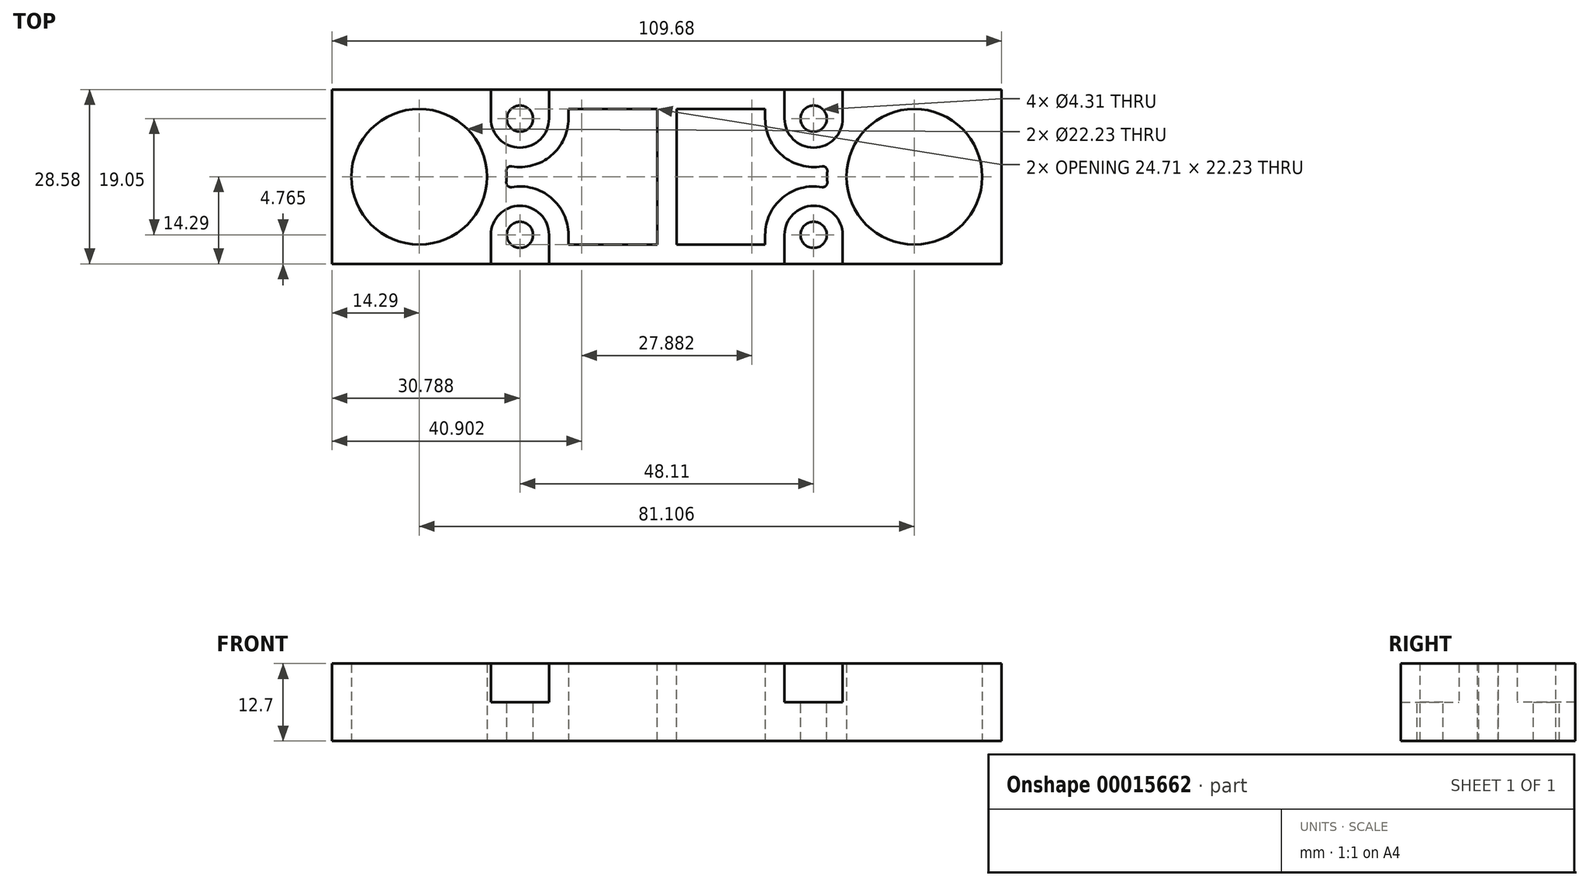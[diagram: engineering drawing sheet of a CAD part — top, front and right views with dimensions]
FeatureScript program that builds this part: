
annotation { "Feature Type Name" : "Feature", "Feature Type Description" : "" }
export const myFeature = defineFeature(function(context is Context, id is Id, definition is map)
    precondition{}
    {
        {
            var Q0;
            Q0=qCreatedBy(makeId("Top.planeOp"),FACE);
            var sketch = newSketch(context, id + "F0", { "sketchPlane" : qUnion([Q0])});
            skCircle(sketch, "E0", {"center": v(0, 0) * mm, "radius": 11.11 * mm});
            skLineSegment(sketch, "E1", {"start": v(0, 0) * mm, "end": v(81.1, 0) * mm, "construction": true});
            skLineSegment(sketch, "E2.left", {"start": v(-14.29, 14.29) * mm, "end": v(-14.29, -14.29) * mm});
            skLineSegment(sketch, "E2.right", {"start": v(95.4, 14.29) * mm, "end": v(95.4, -14.29) * mm});
            skPoint(sketch, "E2.middle", {"position": v(40.55, 0) * mm});
            skLineSegment(sketch, "E3", {"start": v(81.1, 0) * mm, "end": v(95.4, 0) * mm, "construction": true});
            skLineSegment(sketch, "E4", {"start": v(0, 0) * mm, "end": v(-14.29, 0) * mm, "construction": true});
            skCircle(sketch, "E5", {"center": v(81.1, 0) * mm, "radius": 11.11 * mm});
            skLineSegment(sketch, "E6", {"start": v(-14.29, 14.29) * mm, "end": v(11.74, 14.29) * mm});
            skLineSegment(sketch, "E7", {"start": v(95.4, 14.29) * mm, "end": v(69.37, 14.29) * mm});
            skLineSegment(sketch, "E8.bottom", {"start": v(11.74, 14.29) * mm, "end": v(21.26, 14.29) * mm, "construction": true});
            skLineSegment(sketch, "E8.top", {"start": v(11.74, 9.53) * mm, "end": v(21.26, 9.53) * mm, "construction": true});
            skLineSegment(sketch, "E8.left", {"start": v(11.74, 14.29) * mm, "end": v(11.74, 9.52) * mm});
            skLineSegment(sketch, "E8.right", {"start": v(21.26, 14.29) * mm, "end": v(21.26, 9.52) * mm});
            skLineSegment(sketch, "E9.bottom", {"start": v(69.37, 14.29) * mm, "end": v(59.85, 14.29) * mm, "construction": true});
            skLineSegment(sketch, "E9.top", {"start": v(69.37, 9.52) * mm, "end": v(59.85, 9.52) * mm, "construction": true});
            skLineSegment(sketch, "E9.left", {"start": v(69.37, 14.29) * mm, "end": v(69.37, 9.52) * mm});
            skLineSegment(sketch, "E9.right", {"start": v(59.85, 14.29) * mm, "end": v(59.85, 9.53) * mm});
            skCircle(sketch, "E10", {"center": v(16.5, 9.53) * mm, "radius": 7.94 * mm, "construction": true});
            skArc(sketch, "E11", {"start": v(21.26, 9.52) * mm, "mid": v(16.5, 14.29) * mm, "end": v(11.74, 9.53) * mm, "construction": true});
            skArc(sketch, "E12", {"start": v(11.74, 9.52) * mm, "mid": v(16.5, 4.76) * mm, "end": v(21.26, 9.52) * mm});
            skArc(sketch, "E13", {"start": v(59.85, 9.53) * mm, "mid": v(64.6, 4.76) * mm, "end": v(69.37, 9.52) * mm});
            skLineSegment(sketch, "E14", {"start": v(21.26, 14.29) * mm, "end": v(59.85, 14.29) * mm});
            skLineSegment(sketch, "E15", {"start": v(-14.29, -14.29) * mm, "end": v(11.74, -14.29) * mm});
            skLineSegment(sketch, "E16", {"start": v(95.4, -14.29) * mm, "end": v(69.37, -14.29) * mm});
            skLineSegment(sketch, "E17.bottom", {"start": v(11.74, -14.29) * mm, "end": v(21.26, -14.29) * mm, "construction": true});
            skLineSegment(sketch, "E17.top", {"start": v(11.74, -9.52) * mm, "end": v(21.26, -9.52) * mm, "construction": true});
            skLineSegment(sketch, "E17.left", {"start": v(11.74, -14.29) * mm, "end": v(11.74, -9.52) * mm});
            skLineSegment(sketch, "E17.right", {"start": v(21.26, -14.29) * mm, "end": v(21.26, -9.53) * mm});
            skLineSegment(sketch, "E18.bottom", {"start": v(69.37, -14.29) * mm, "end": v(59.85, -14.29) * mm, "construction": true});
            skLineSegment(sketch, "E18.top", {"start": v(69.37, -9.52) * mm, "end": v(59.85, -9.52) * mm, "construction": true});
            skLineSegment(sketch, "E18.left", {"start": v(69.37, -14.29) * mm, "end": v(69.37, -9.52) * mm});
            skLineSegment(sketch, "E18.right", {"start": v(59.85, -14.29) * mm, "end": v(59.85, -9.52) * mm});
            skLineSegment(sketch, "E19", {"start": v(21.26, -14.29) * mm, "end": v(59.85, -14.29) * mm});
            skArc(sketch, "E20", {"start": v(21.26, -9.53) * mm, "mid": v(16.5, -4.76) * mm, "end": v(11.74, -9.52) * mm});
            skArc(sketch, "E21", {"start": v(69.37, -9.52) * mm, "mid": v(64.6, -4.76) * mm, "end": v(59.85, -9.52) * mm});
            skSolve(sketch);
        }
        {
            var Q0;
            Q0=qSketchRegion(id+"F0",true);
            extrude(context, id + "F1", {"entities" : qUnion([Q0]), "depth" : 6.35 * mm});
        }
        {
            var Q0;
            Q0=makeQuery(id+"F1.opExtrude","CAP_FACE",FACE,{"disambiguationData":[OSD([sQuery(id+"F0.wireOp",EDGE,"E0"),sQuery(id+"F0.wireOp",EDGE,"E2.left"),sQuery(id+"F0.wireOp",EDGE,"E2.right"),sQuery(id+"F0.wireOp",EDGE,"E5"),sQuery(id+"F0.wireOp",EDGE,"E6"),sQuery(id+"F0.wireOp",EDGE,"E7"),sQuery(id+"F0.wireOp",EDGE,"E8.left"),sQuery(id+"F0.wireOp",EDGE,"E8.right"),sQuery(id+"F0.wireOp",EDGE,"E9.left"),sQuery(id+"F0.wireOp",EDGE,"E9.right"),sQuery(id+"F0.wireOp",EDGE,"E12"),sQuery(id+"F0.wireOp",EDGE,"E13"),sQuery(id+"F0.wireOp",EDGE,"E14"),sQuery(id+"F0.wireOp",EDGE,"E15"),sQuery(id+"F0.wireOp",EDGE,"E16"),sQuery(id+"F0.wireOp",EDGE,"E17.left"),sQuery(id+"F0.wireOp",EDGE,"E17.right"),sQuery(id+"F0.wireOp",EDGE,"E18.left"),sQuery(id+"F0.wireOp",EDGE,"E18.right"),sQuery(id+"F0.wireOp",EDGE,"E19"),sQuery(id+"F0.wireOp",EDGE,"E20"),sQuery(id+"F0.wireOp",EDGE,"E21")])],"isStart":false});
            shell(context, id + "F2", {"entities" : qUnion([Q0]), "thickness" : 3.17 * mm});
        }
        {
            var Q0;
            Q0=makeQuery(id+"F2.opShell","OFFSET_FACE",FACE,{"disambiguationData":[OSD([sQuery(id+"F0.wireOp",EDGE,"E0"),sQuery(id+"F0.wireOp",EDGE,"E2.left"),sQuery(id+"F0.wireOp",EDGE,"E2.right"),sQuery(id+"F0.wireOp",EDGE,"E5"),sQuery(id+"F0.wireOp",EDGE,"E6"),sQuery(id+"F0.wireOp",EDGE,"E7"),sQuery(id+"F0.wireOp",EDGE,"E8.left"),sQuery(id+"F0.wireOp",EDGE,"E8.right"),sQuery(id+"F0.wireOp",EDGE,"E9.left"),sQuery(id+"F0.wireOp",EDGE,"E9.right"),sQuery(id+"F0.wireOp",EDGE,"E12"),sQuery(id+"F0.wireOp",EDGE,"E13"),sQuery(id+"F0.wireOp",EDGE,"E14"),sQuery(id+"F0.wireOp",EDGE,"E15"),sQuery(id+"F0.wireOp",EDGE,"E16"),sQuery(id+"F0.wireOp",EDGE,"E17.left"),sQuery(id+"F0.wireOp",EDGE,"E17.right"),sQuery(id+"F0.wireOp",EDGE,"E18.left"),sQuery(id+"F0.wireOp",EDGE,"E18.right"),sQuery(id+"F0.wireOp",EDGE,"E19"),sQuery(id+"F0.wireOp",EDGE,"E20"),sQuery(id+"F0.wireOp",EDGE,"E21")]),OD(0.0)]});
            var Q1;
            Q1=makeQuery(id+"F2.opShell","OFFSET_FACE",FACE,{"disambiguationData":[OSD([sQuery(id+"F0.wireOp",EDGE,"E0"),sQuery(id+"F0.wireOp",EDGE,"E2.left"),sQuery(id+"F0.wireOp",EDGE,"E2.right"),sQuery(id+"F0.wireOp",EDGE,"E5"),sQuery(id+"F0.wireOp",EDGE,"E6"),sQuery(id+"F0.wireOp",EDGE,"E7"),sQuery(id+"F0.wireOp",EDGE,"E8.left"),sQuery(id+"F0.wireOp",EDGE,"E8.right"),sQuery(id+"F0.wireOp",EDGE,"E9.left"),sQuery(id+"F0.wireOp",EDGE,"E9.right"),sQuery(id+"F0.wireOp",EDGE,"E12"),sQuery(id+"F0.wireOp",EDGE,"E13"),sQuery(id+"F0.wireOp",EDGE,"E14"),sQuery(id+"F0.wireOp",EDGE,"E15"),sQuery(id+"F0.wireOp",EDGE,"E16"),sQuery(id+"F0.wireOp",EDGE,"E17.left"),sQuery(id+"F0.wireOp",EDGE,"E17.right"),sQuery(id+"F0.wireOp",EDGE,"E18.left"),sQuery(id+"F0.wireOp",EDGE,"E18.right"),sQuery(id+"F0.wireOp",EDGE,"E19"),sQuery(id+"F0.wireOp",EDGE,"E20"),sQuery(id+"F0.wireOp",EDGE,"E21")]),OD(3.0)]});
            var Q2;
            Q2=makeQuery(id+"F2.opShell","OFFSET_FACE",FACE,{"disambiguationData":[OSD([sQuery(id+"F0.wireOp",EDGE,"E0"),sQuery(id+"F0.wireOp",EDGE,"E2.left"),sQuery(id+"F0.wireOp",EDGE,"E2.right"),sQuery(id+"F0.wireOp",EDGE,"E5"),sQuery(id+"F0.wireOp",EDGE,"E6"),sQuery(id+"F0.wireOp",EDGE,"E7"),sQuery(id+"F0.wireOp",EDGE,"E8.left"),sQuery(id+"F0.wireOp",EDGE,"E8.right"),sQuery(id+"F0.wireOp",EDGE,"E9.left"),sQuery(id+"F0.wireOp",EDGE,"E9.right"),sQuery(id+"F0.wireOp",EDGE,"E12"),sQuery(id+"F0.wireOp",EDGE,"E13"),sQuery(id+"F0.wireOp",EDGE,"E14"),sQuery(id+"F0.wireOp",EDGE,"E15"),sQuery(id+"F0.wireOp",EDGE,"E16"),sQuery(id+"F0.wireOp",EDGE,"E17.left"),sQuery(id+"F0.wireOp",EDGE,"E17.right"),sQuery(id+"F0.wireOp",EDGE,"E18.left"),sQuery(id+"F0.wireOp",EDGE,"E18.right"),sQuery(id+"F0.wireOp",EDGE,"E19"),sQuery(id+"F0.wireOp",EDGE,"E20"),sQuery(id+"F0.wireOp",EDGE,"E21")]),OD(4.0)]});
            var Q3;
            Q3=makeQuery(id+"F2.opShell","OFFSET_FACE",FACE,{"disambiguationData":[OSD([sQuery(id+"F0.wireOp",EDGE,"E0"),sQuery(id+"F0.wireOp",EDGE,"E2.left"),sQuery(id+"F0.wireOp",EDGE,"E2.right"),sQuery(id+"F0.wireOp",EDGE,"E5"),sQuery(id+"F0.wireOp",EDGE,"E6"),sQuery(id+"F0.wireOp",EDGE,"E7"),sQuery(id+"F0.wireOp",EDGE,"E8.left"),sQuery(id+"F0.wireOp",EDGE,"E8.right"),sQuery(id+"F0.wireOp",EDGE,"E9.left"),sQuery(id+"F0.wireOp",EDGE,"E9.right"),sQuery(id+"F0.wireOp",EDGE,"E12"),sQuery(id+"F0.wireOp",EDGE,"E13"),sQuery(id+"F0.wireOp",EDGE,"E14"),sQuery(id+"F0.wireOp",EDGE,"E15"),sQuery(id+"F0.wireOp",EDGE,"E16"),sQuery(id+"F0.wireOp",EDGE,"E17.left"),sQuery(id+"F0.wireOp",EDGE,"E17.right"),sQuery(id+"F0.wireOp",EDGE,"E18.left"),sQuery(id+"F0.wireOp",EDGE,"E18.right"),sQuery(id+"F0.wireOp",EDGE,"E19"),sQuery(id+"F0.wireOp",EDGE,"E20"),sQuery(id+"F0.wireOp",EDGE,"E21")]),OD(1.0)]});
            var Q4;
            Q4=makeQuery(id+"F1.opExtrude","CAP_FACE",FACE,{"disambiguationData":[OSD([sQuery(id+"F0.wireOp",EDGE,"E0"),sQuery(id+"F0.wireOp",EDGE,"E2.left"),sQuery(id+"F0.wireOp",EDGE,"E2.right"),sQuery(id+"F0.wireOp",EDGE,"E5"),sQuery(id+"F0.wireOp",EDGE,"E6"),sQuery(id+"F0.wireOp",EDGE,"E7"),sQuery(id+"F0.wireOp",EDGE,"E8.left"),sQuery(id+"F0.wireOp",EDGE,"E8.right"),sQuery(id+"F0.wireOp",EDGE,"E9.left"),sQuery(id+"F0.wireOp",EDGE,"E9.right"),sQuery(id+"F0.wireOp",EDGE,"E12"),sQuery(id+"F0.wireOp",EDGE,"E13"),sQuery(id+"F0.wireOp",EDGE,"E14"),sQuery(id+"F0.wireOp",EDGE,"E15"),sQuery(id+"F0.wireOp",EDGE,"E16"),sQuery(id+"F0.wireOp",EDGE,"E17.left"),sQuery(id+"F0.wireOp",EDGE,"E17.right"),sQuery(id+"F0.wireOp",EDGE,"E18.left"),sQuery(id+"F0.wireOp",EDGE,"E18.right"),sQuery(id+"F0.wireOp",EDGE,"E19"),sQuery(id+"F0.wireOp",EDGE,"E20"),sQuery(id+"F0.wireOp",EDGE,"E21")])],"isStart":false});
            extrude(context, id + "F3", {"entities" : qUnion([Q0, Q1, Q2, Q3]), "operationType" : NewBodyOperationType.ADD, "endBound" : BoundingType.UP_TO_SURFACE, "endBoundEntityFace" : qUnion([Q4]), "depth" : 25.4 * mm});
        }
        {
            var Q0;
            Q0=makeQuery(id+"F2.opShell","OFFSET_FACE",FACE,{"disambiguationData":[OSD([sQuery(id+"F0.wireOp",EDGE,"E0"),sQuery(id+"F0.wireOp",EDGE,"E2.left"),sQuery(id+"F0.wireOp",EDGE,"E2.right"),sQuery(id+"F0.wireOp",EDGE,"E5"),sQuery(id+"F0.wireOp",EDGE,"E6"),sQuery(id+"F0.wireOp",EDGE,"E7"),sQuery(id+"F0.wireOp",EDGE,"E8.left"),sQuery(id+"F0.wireOp",EDGE,"E8.right"),sQuery(id+"F0.wireOp",EDGE,"E9.left"),sQuery(id+"F0.wireOp",EDGE,"E9.right"),sQuery(id+"F0.wireOp",EDGE,"E12"),sQuery(id+"F0.wireOp",EDGE,"E13"),sQuery(id+"F0.wireOp",EDGE,"E14"),sQuery(id+"F0.wireOp",EDGE,"E15"),sQuery(id+"F0.wireOp",EDGE,"E16"),sQuery(id+"F0.wireOp",EDGE,"E17.left"),sQuery(id+"F0.wireOp",EDGE,"E17.right"),sQuery(id+"F0.wireOp",EDGE,"E18.left"),sQuery(id+"F0.wireOp",EDGE,"E18.right"),sQuery(id+"F0.wireOp",EDGE,"E19"),sQuery(id+"F0.wireOp",EDGE,"E20"),sQuery(id+"F0.wireOp",EDGE,"E21")]),OD(2.0)]});
            var Q1;
            Q1=makeQuery(id+"F1.opExtrude","CAP_FACE",FACE,{"disambiguationData":[OSD([sQuery(id+"F0.wireOp",EDGE,"E0"),sQuery(id+"F0.wireOp",EDGE,"E2.left"),sQuery(id+"F0.wireOp",EDGE,"E2.right"),sQuery(id+"F0.wireOp",EDGE,"E5"),sQuery(id+"F0.wireOp",EDGE,"E6"),sQuery(id+"F0.wireOp",EDGE,"E7"),sQuery(id+"F0.wireOp",EDGE,"E8.left"),sQuery(id+"F0.wireOp",EDGE,"E8.right"),sQuery(id+"F0.wireOp",EDGE,"E9.left"),sQuery(id+"F0.wireOp",EDGE,"E9.right"),sQuery(id+"F0.wireOp",EDGE,"E12"),sQuery(id+"F0.wireOp",EDGE,"E13"),sQuery(id+"F0.wireOp",EDGE,"E14"),sQuery(id+"F0.wireOp",EDGE,"E15"),sQuery(id+"F0.wireOp",EDGE,"E16"),sQuery(id+"F0.wireOp",EDGE,"E17.left"),sQuery(id+"F0.wireOp",EDGE,"E17.right"),sQuery(id+"F0.wireOp",EDGE,"E18.left"),sQuery(id+"F0.wireOp",EDGE,"E18.right"),sQuery(id+"F0.wireOp",EDGE,"E19"),sQuery(id+"F0.wireOp",EDGE,"E20"),sQuery(id+"F0.wireOp",EDGE,"E21")])],"isStart":true});
            extrude(context, id + "F4", {"entities" : qUnion([Q0]), "operationType" : NewBodyOperationType.REMOVE, "endBound" : BoundingType.UP_TO_SURFACE, "oppositeDirection" : true, "endBoundEntityFace" : qUnion([Q1]), "depth" : 25.4 * mm});
        }
        {
            var Q0;
            Q0=makeQuery(id+"F1.opExtrude","CAP_FACE",FACE,{"disambiguationData":[OSD([sQuery(id+"F0.wireOp",EDGE,"E0"),sQuery(id+"F0.wireOp",EDGE,"E2.left"),sQuery(id+"F0.wireOp",EDGE,"E2.right"),sQuery(id+"F0.wireOp",EDGE,"E5"),sQuery(id+"F0.wireOp",EDGE,"E6"),sQuery(id+"F0.wireOp",EDGE,"E7"),sQuery(id+"F0.wireOp",EDGE,"E8.left"),sQuery(id+"F0.wireOp",EDGE,"E8.right"),sQuery(id+"F0.wireOp",EDGE,"E9.left"),sQuery(id+"F0.wireOp",EDGE,"E9.right"),sQuery(id+"F0.wireOp",EDGE,"E12"),sQuery(id+"F0.wireOp",EDGE,"E13"),sQuery(id+"F0.wireOp",EDGE,"E14"),sQuery(id+"F0.wireOp",EDGE,"E15"),sQuery(id+"F0.wireOp",EDGE,"E16"),sQuery(id+"F0.wireOp",EDGE,"E17.left"),sQuery(id+"F0.wireOp",EDGE,"E17.right"),sQuery(id+"F0.wireOp",EDGE,"E18.left"),sQuery(id+"F0.wireOp",EDGE,"E18.right"),sQuery(id+"F0.wireOp",EDGE,"E19"),sQuery(id+"F0.wireOp",EDGE,"E20"),sQuery(id+"F0.wireOp",EDGE,"E21")])],"isStart":true});
            var sketch = newSketch(context, id + "F5", { "sketchPlane" : qUnion([Q0])});
            skLineSegment(sketch, "E22.bottom", {"start": v(11.74, -14.29) * mm, "end": v(69.37, -14.29) * mm});
            skLineSegment(sketch, "E22.top", {"start": v(11.74, 14.29) * mm, "end": v(69.37, 14.29) * mm});
            skLineSegment(sketch, "E22.left", {"start": v(11.74, -14.29) * mm, "end": v(11.74, 14.29) * mm, "construction": true});
            skLineSegment(sketch, "E22.right", {"start": v(69.37, -14.29) * mm, "end": v(69.37, 14.29) * mm, "construction": true});
            skCircle(sketch, "E23", {"center": v(16.5, 9.52) * mm, "radius": 2.15 * mm});
            skCircle(sketch, "E24", {"center": v(16.5, -9.53) * mm, "radius": 2.15 * mm});
            skCircle(sketch, "E25", {"center": v(64.6, 9.52) * mm, "radius": 2.15 * mm});
            skCircle(sketch, "E26", {"center": v(64.6, -9.53) * mm, "radius": 2.15 * mm});
            skSolve(sketch);
        }
        {
            var Q0;
            {var subQ19=sQuery(id+"F0.wireOp",EDGE,"E0");var subQ20=makeQuery(id+"F1.opExtrude","CAP_EDGE",EDGE,{"disambiguationData":[OSD([subQ19])],"isStart":true});Q0=makeQuery(id+"F5.imprint","IMPRINT",FACE,{"disambiguationData":[TD([[makeQuery(id+"F5.imprint","IMPRINT",EDGE,{"derivedFrom":subQ20}),1.0]])]});}
            var Q1;
            Q1=makeQuery(id+"F5.imprint","IMPRINT",FACE,{"disambiguationData":[TD([[makeQuery(id+"F5.imprint","IMPRINT",EDGE,{"derivedFrom":sQuery(id+"F5.wireOp",EDGE,"E24")}),-1.0]])]});
            var Q2;
            Q2=makeQuery(id+"F5.imprint","IMPRINT",FACE,{"disambiguationData":[TD([[makeQuery(id+"F5.imprint","IMPRINT",EDGE,{"derivedFrom":sQuery(id+"F5.wireOp",EDGE,"E26")}),-1.0]])]});
            var Q3;
            Q3=makeQuery(id+"F5.imprint","IMPRINT",FACE,{"disambiguationData":[TD([[makeQuery(id+"F5.imprint","IMPRINT",EDGE,{"derivedFrom":sQuery(id+"F5.wireOp",EDGE,"E25")}),-1.0]])]});
            var Q4;
            Q4=makeQuery(id+"F5.imprint","IMPRINT",FACE,{"disambiguationData":[TD([[makeQuery(id+"F5.imprint","IMPRINT",EDGE,{"derivedFrom":sQuery(id+"F5.wireOp",EDGE,"E23")}),-1.0]])]});
            extrude(context, id + "F6", {"entities" : qUnion([Q0, Q1, Q2, Q3, Q4]), "operationType" : NewBodyOperationType.ADD, "depth" : 6.35 * mm});
        }
        {
            var Q0;
            {var subQ0=sQuery(id+"F0.wireOp",EDGE,"E21");var subQ1=sQuery(id+"F0.wireOp",EDGE,"E20");var subQ2=sQuery(id+"F0.wireOp",EDGE,"E19");var subQ3=sQuery(id+"F0.wireOp",EDGE,"E18.right");var subQ4=sQuery(id+"F0.wireOp",EDGE,"E18.left");var subQ5=sQuery(id+"F0.wireOp",EDGE,"E17.right");var subQ6=sQuery(id+"F0.wireOp",EDGE,"E17.left");var subQ7=sQuery(id+"F0.wireOp",EDGE,"E16");var subQ8=sQuery(id+"F0.wireOp",EDGE,"E15");var subQ9=sQuery(id+"F0.wireOp",EDGE,"E14");var subQ10=sQuery(id+"F0.wireOp",EDGE,"E13");var subQ11=sQuery(id+"F0.wireOp",EDGE,"E12");var subQ12=sQuery(id+"F0.wireOp",EDGE,"E9.right");var subQ13=sQuery(id+"F0.wireOp",EDGE,"E9.left");var subQ14=sQuery(id+"F0.wireOp",EDGE,"E8.right");var subQ15=sQuery(id+"F0.wireOp",EDGE,"E8.left");var subQ16=sQuery(id+"F0.wireOp",EDGE,"E7");var subQ17=sQuery(id+"F0.wireOp",EDGE,"E6");var subQ18=sQuery(id+"F0.wireOp",EDGE,"E5");var subQ19=sQuery(id+"F0.wireOp",EDGE,"E2.right");var subQ20=sQuery(id+"F0.wireOp",EDGE,"E2.left");var subQ21=sQuery(id+"F0.wireOp",EDGE,"E0");Q0=makeQuery(id+"F3.boolean.opBoolean","MERGE",FACE,{"derivedFrom":[makeQuery(id+"F1.opExtrude","CAP_FACE",FACE,{"disambiguationData":[OSD([subQ21,subQ20,subQ19,subQ18,subQ17,subQ16,subQ15,subQ14,subQ13,subQ12,subQ11,subQ10,subQ9,subQ8,subQ7,subQ6,subQ5,subQ4,subQ3,subQ2,subQ1,subQ0])],"isStart":false}),makeQuery(id+"F3.opExtrude","CAP_FACE",FACE,{"disambiguationData":[OSD([subQ21,subQ20,subQ19,subQ18,subQ17,subQ16,subQ15,subQ14,subQ13,subQ12,subQ11,subQ10,subQ9,subQ8,subQ7,subQ6,subQ5,subQ4,subQ3,subQ2,subQ1,subQ0]),ownerDisambiguation([makeQuery(id+"F3.opExtrude","SWEPT_BODY",BODY,{"disambiguationData":[OSD([subQ21,subQ20,subQ19,subQ18,subQ17,subQ16,subQ15,subQ14,subQ13,subQ12,subQ11,subQ10,subQ9,subQ8,subQ7,subQ6,subQ5,subQ4,subQ3,subQ2,subQ1,subQ0]),TDD([makeQuery(id+"F2.opShell","OFFSET_FACE",FACE,{"disambiguationData":[OSD([subQ21,subQ20,subQ19,subQ18,subQ17,subQ16,subQ15,subQ14,subQ13,subQ12,subQ11,subQ10,subQ9,subQ8,subQ7,subQ6,subQ5,subQ4,subQ3,subQ2,subQ1,subQ0]),OD(0.0)]})])]})])],"isStart":false}),makeQuery(id+"F3.opExtrude","CAP_FACE",FACE,{"disambiguationData":[OSD([subQ21,subQ20,subQ19,subQ18,subQ17,subQ16,subQ15,subQ14,subQ13,subQ12,subQ11,subQ10,subQ9,subQ8,subQ7,subQ6,subQ5,subQ4,subQ3,subQ2,subQ1,subQ0]),ownerDisambiguation([makeQuery(id+"F3.opExtrude","SWEPT_BODY",BODY,{"disambiguationData":[OSD([subQ21,subQ20,subQ19,subQ18,subQ17,subQ16,subQ15,subQ14,subQ13,subQ12,subQ11,subQ10,subQ9,subQ8,subQ7,subQ6,subQ5,subQ4,subQ3,subQ2,subQ1,subQ0]),TDD([makeQuery(id+"F2.opShell","OFFSET_FACE",FACE,{"disambiguationData":[OSD([subQ21,subQ20,subQ19,subQ18,subQ17,subQ16,subQ15,subQ14,subQ13,subQ12,subQ11,subQ10,subQ9,subQ8,subQ7,subQ6,subQ5,subQ4,subQ3,subQ2,subQ1,subQ0]),OD(1.0)]})])]})])],"isStart":false}),makeQuery(id+"F3.opExtrude","CAP_FACE",FACE,{"disambiguationData":[OSD([subQ21,subQ20,subQ19,subQ18,subQ17,subQ16,subQ15,subQ14,subQ13,subQ12,subQ11,subQ10,subQ9,subQ8,subQ7,subQ6,subQ5,subQ4,subQ3,subQ2,subQ1,subQ0]),ownerDisambiguation([makeQuery(id+"F3.opExtrude","SWEPT_BODY",BODY,{"disambiguationData":[OSD([subQ21,subQ20,subQ19,subQ18,subQ17,subQ16,subQ15,subQ14,subQ13,subQ12,subQ11,subQ10,subQ9,subQ8,subQ7,subQ6,subQ5,subQ4,subQ3,subQ2,subQ1,subQ0]),TDD([makeQuery(id+"F2.opShell","OFFSET_FACE",FACE,{"disambiguationData":[OSD([subQ21,subQ20,subQ19,subQ18,subQ17,subQ16,subQ15,subQ14,subQ13,subQ12,subQ11,subQ10,subQ9,subQ8,subQ7,subQ6,subQ5,subQ4,subQ3,subQ2,subQ1,subQ0]),OD(3.0)]})])]})])],"isStart":false}),makeQuery(id+"F3.opExtrude","CAP_FACE",FACE,{"disambiguationData":[OSD([subQ21,subQ20,subQ19,subQ18,subQ17,subQ16,subQ15,subQ14,subQ13,subQ12,subQ11,subQ10,subQ9,subQ8,subQ7,subQ6,subQ5,subQ4,subQ3,subQ2,subQ1,subQ0]),ownerDisambiguation([makeQuery(id+"F3.opExtrude","SWEPT_BODY",BODY,{"disambiguationData":[OSD([subQ21,subQ20,subQ19,subQ18,subQ17,subQ16,subQ15,subQ14,subQ13,subQ12,subQ11,subQ10,subQ9,subQ8,subQ7,subQ6,subQ5,subQ4,subQ3,subQ2,subQ1,subQ0]),TDD([makeQuery(id+"F2.opShell","OFFSET_FACE",FACE,{"disambiguationData":[OSD([subQ21,subQ20,subQ19,subQ18,subQ17,subQ16,subQ15,subQ14,subQ13,subQ12,subQ11,subQ10,subQ9,subQ8,subQ7,subQ6,subQ5,subQ4,subQ3,subQ2,subQ1,subQ0]),OD(4.0)]})])]})])],"isStart":false})]});}
            var sketch = newSketch(context, id + "F7", { "sketchPlane" : qUnion([Q0])});
            skLineSegment(sketch, "E27.bottom", {"start": v(38.97, 11.11) * mm, "end": v(42.14, 11.11) * mm});
            skLineSegment(sketch, "E27.top", {"start": v(38.97, -11.11) * mm, "end": v(42.14, -11.11) * mm});
            skLineSegment(sketch, "E27.left", {"start": v(38.97, 11.11) * mm, "end": v(38.97, -11.11) * mm});
            skLineSegment(sketch, "E27.right", {"start": v(42.14, 11.11) * mm, "end": v(42.14, -11.11) * mm});
            skPoint(sketch, "E28", {"position": v(40.55, 11.11) * mm});
            skSolve(sketch);
        }
        {
            var Q0;
            Q0=qSketchRegion(id+"F7",true);
            var Q1;
            Q1=makeQuery(id+"F6.opExtrude","CAP_FACE",FACE,{"disambiguationData":[OSD([sQuery(id+"F0.wireOp",EDGE,"E0"),sQuery(id+"F0.wireOp",EDGE,"E2.left"),sQuery(id+"F0.wireOp",EDGE,"E2.right"),sQuery(id+"F0.wireOp",EDGE,"E5"),sQuery(id+"F0.wireOp",EDGE,"E6"),sQuery(id+"F0.wireOp",EDGE,"E7"),sQuery(id+"F0.wireOp",EDGE,"E8.left"),sQuery(id+"F0.wireOp",EDGE,"E8.right"),sQuery(id+"F0.wireOp",EDGE,"E9.left"),sQuery(id+"F0.wireOp",EDGE,"E9.right"),sQuery(id+"F0.wireOp",EDGE,"E12"),sQuery(id+"F0.wireOp",EDGE,"E13"),sQuery(id+"F0.wireOp",EDGE,"E14"),sQuery(id+"F0.wireOp",EDGE,"E15"),sQuery(id+"F0.wireOp",EDGE,"E16"),sQuery(id+"F0.wireOp",EDGE,"E17.left"),sQuery(id+"F0.wireOp",EDGE,"E17.right"),sQuery(id+"F0.wireOp",EDGE,"E18.left"),sQuery(id+"F0.wireOp",EDGE,"E18.right"),sQuery(id+"F0.wireOp",EDGE,"E19"),sQuery(id+"F0.wireOp",EDGE,"E20"),sQuery(id+"F0.wireOp",EDGE,"E21"),sQuery(id+"F5.wireOp",EDGE,"E22.bottom"),sQuery(id+"F5.wireOp",EDGE,"E22.top"),sQuery(id+"F5.wireOp",EDGE,"E23"),sQuery(id+"F5.wireOp",EDGE,"E24"),sQuery(id+"F5.wireOp",EDGE,"E25"),sQuery(id+"F5.wireOp",EDGE,"E26")])],"isStart":false});
            extrude(context, id + "F8", {"entities" : qUnion([Q0]), "operationType" : NewBodyOperationType.ADD, "endBound" : BoundingType.UP_TO_SURFACE, "oppositeDirection" : true, "endBoundEntityFace" : qUnion([Q1]), "depth" : 25.4 * mm});
        }
        {
            var Q0;
            {var subQ0=sQuery(id+"F0.wireOp",EDGE,"E0");var subQ1=sQuery(id+"F0.wireOp",EDGE,"E21");var subQ2=sQuery(id+"F0.wireOp",EDGE,"E20");var subQ3=sQuery(id+"F0.wireOp",EDGE,"E19");var subQ4=sQuery(id+"F0.wireOp",EDGE,"E18.right");var subQ5=sQuery(id+"F0.wireOp",EDGE,"E18.left");var subQ6=sQuery(id+"F0.wireOp",EDGE,"E17.right");var subQ7=sQuery(id+"F0.wireOp",EDGE,"E17.left");var subQ8=sQuery(id+"F0.wireOp",EDGE,"E16");var subQ9=sQuery(id+"F0.wireOp",EDGE,"E15");var subQ10=sQuery(id+"F0.wireOp",EDGE,"E14");var subQ11=sQuery(id+"F0.wireOp",EDGE,"E13");var subQ12=sQuery(id+"F0.wireOp",EDGE,"E12");var subQ13=sQuery(id+"F0.wireOp",EDGE,"E9.right");var subQ14=sQuery(id+"F0.wireOp",EDGE,"E9.left");var subQ15=sQuery(id+"F0.wireOp",EDGE,"E8.right");var subQ16=sQuery(id+"F0.wireOp",EDGE,"E8.left");var subQ17=sQuery(id+"F0.wireOp",EDGE,"E7");var subQ18=sQuery(id+"F0.wireOp",EDGE,"E6");var subQ19=sQuery(id+"F0.wireOp",EDGE,"E5");var subQ20=sQuery(id+"F0.wireOp",EDGE,"E2.right");var subQ21=sQuery(id+"F0.wireOp",EDGE,"E2.left");var subQ22=makeQuery(id+"F1.opExtrude","CAP_FACE",FACE,{"disambiguationData":[OSD([subQ0,subQ21,subQ20,subQ19,subQ18,subQ17,subQ16,subQ15,subQ14,subQ13,subQ12,subQ11,subQ10,subQ9,subQ8,subQ7,subQ6,subQ5,subQ4,subQ3,subQ2,subQ1])],"isStart":true});var subQ23=makeQuery(id+"F1.opExtrude","SWEPT_FACE",FACE,{"disambiguationData":[OSD([subQ12])]});var subQ24=makeQuery(id+"F1.opExtrude","SWEPT_FACE",FACE,{"disambiguationData":[OSD([subQ0])]});Q0=makeQuery(id+"F6.boolean.opBoolean","MERGE",EDGE,{"derivedFrom":[makeQuery(id+"F4.boolean.opBoolean","MERGE",EDGE,{"derivedFrom":[makeQuery(id+"F2.opShell","TWEAK_EDGE",EDGE,{"derivedFrom":[subQ24,subQ23]}),makeQuery(id+"F4.opExtrude","SWEPT_EDGE",EDGE,{"disambiguationData":[OSD([subQ0,subQ21,subQ20,subQ19,subQ18,subQ17,subQ16,subQ15,subQ14,subQ13,subQ12,subQ11,subQ10,subQ9,subQ8,subQ7,subQ6,subQ5,subQ4,subQ3,subQ2,subQ1]),TDD([makeQuery(id+"F2.opShell","TWEAK_VERTEX",VERTEX,{"derivedFrom":[subQ24,subQ22,subQ23]})])]})]}),makeQuery(id+"F6.opExtrude","SWEPT_EDGE",EDGE,{"disambiguationData":[OSD([subQ0,subQ21,subQ20,subQ19,subQ18,subQ17,subQ16,subQ15,subQ14,subQ13,subQ12,subQ11,subQ10,subQ9,subQ8,subQ7,subQ6,subQ5,subQ4,subQ3,subQ2,subQ1]),TDD([makeQuery(id+"F5.imprint","INTERSECT",VERTEX,{"derivedFrom":[makeQuery(id+"F4.boolean.opBoolean","COPY",EDGE,{"derivedFrom":makeQuery(id+"F4.opExtrude","TWEAK_EDGE",EDGE,{"derivedFrom":[subQ22,makeQuery(id+"F2.opShell","OFFSET_EDGE",EDGE,{"disambiguationData":[OSD([subQ12]),TDD([makeQuery(id+"F1.opExtrude","CAP_EDGE",EDGE,{"disambiguationData":[OSD([subQ12])],"isStart":true})])]})]})}),makeQuery(id+"F4.boolean.opBoolean","COPY",EDGE,{"derivedFrom":makeQuery(id+"F4.opExtrude","TWEAK_EDGE",EDGE,{"derivedFrom":[subQ22,makeQuery(id+"F2.opShell","OFFSET_EDGE",EDGE,{"disambiguationData":[OSD([subQ0]),TDD([makeQuery(id+"F1.opExtrude","CAP_EDGE",EDGE,{"disambiguationData":[OSD([subQ0])],"isStart":true})]),OD(0.0)]})]})})]})])]})]});}
            var Q1;
            {var subQ0=sQuery(id+"F0.wireOp",EDGE,"E0");var subQ1=sQuery(id+"F0.wireOp",EDGE,"E21");var subQ2=sQuery(id+"F0.wireOp",EDGE,"E20");var subQ3=sQuery(id+"F0.wireOp",EDGE,"E19");var subQ4=sQuery(id+"F0.wireOp",EDGE,"E18.right");var subQ5=sQuery(id+"F0.wireOp",EDGE,"E18.left");var subQ6=sQuery(id+"F0.wireOp",EDGE,"E17.right");var subQ7=sQuery(id+"F0.wireOp",EDGE,"E17.left");var subQ8=sQuery(id+"F0.wireOp",EDGE,"E16");var subQ9=sQuery(id+"F0.wireOp",EDGE,"E15");var subQ10=sQuery(id+"F0.wireOp",EDGE,"E14");var subQ11=sQuery(id+"F0.wireOp",EDGE,"E13");var subQ12=sQuery(id+"F0.wireOp",EDGE,"E12");var subQ13=sQuery(id+"F0.wireOp",EDGE,"E9.right");var subQ14=sQuery(id+"F0.wireOp",EDGE,"E9.left");var subQ15=sQuery(id+"F0.wireOp",EDGE,"E8.right");var subQ16=sQuery(id+"F0.wireOp",EDGE,"E8.left");var subQ17=sQuery(id+"F0.wireOp",EDGE,"E7");var subQ18=sQuery(id+"F0.wireOp",EDGE,"E6");var subQ19=sQuery(id+"F0.wireOp",EDGE,"E5");var subQ20=sQuery(id+"F0.wireOp",EDGE,"E2.right");var subQ21=sQuery(id+"F0.wireOp",EDGE,"E2.left");var subQ22=makeQuery(id+"F1.opExtrude","CAP_FACE",FACE,{"disambiguationData":[OSD([subQ0,subQ21,subQ20,subQ19,subQ18,subQ17,subQ16,subQ15,subQ14,subQ13,subQ12,subQ11,subQ10,subQ9,subQ8,subQ7,subQ6,subQ5,subQ4,subQ3,subQ2,subQ1])],"isStart":true});var subQ23=makeQuery(id+"F1.opExtrude","SWEPT_FACE",FACE,{"disambiguationData":[OSD([subQ2])]});var subQ24=makeQuery(id+"F1.opExtrude","SWEPT_FACE",FACE,{"disambiguationData":[OSD([subQ0])]});Q1=makeQuery(id+"F6.boolean.opBoolean","MERGE",EDGE,{"derivedFrom":[makeQuery(id+"F4.boolean.opBoolean","MERGE",EDGE,{"derivedFrom":[makeQuery(id+"F2.opShell","TWEAK_EDGE",EDGE,{"derivedFrom":[subQ24,subQ23]}),makeQuery(id+"F4.opExtrude","SWEPT_EDGE",EDGE,{"disambiguationData":[OSD([subQ0,subQ21,subQ20,subQ19,subQ18,subQ17,subQ16,subQ15,subQ14,subQ13,subQ12,subQ11,subQ10,subQ9,subQ8,subQ7,subQ6,subQ5,subQ4,subQ3,subQ2,subQ1]),TDD([makeQuery(id+"F2.opShell","TWEAK_VERTEX",VERTEX,{"derivedFrom":[subQ24,subQ22,subQ23]})])]})]}),makeQuery(id+"F6.opExtrude","SWEPT_EDGE",EDGE,{"disambiguationData":[OSD([subQ0,subQ21,subQ20,subQ19,subQ18,subQ17,subQ16,subQ15,subQ14,subQ13,subQ12,subQ11,subQ10,subQ9,subQ8,subQ7,subQ6,subQ5,subQ4,subQ3,subQ2,subQ1]),TDD([makeQuery(id+"F5.imprint","INTERSECT",VERTEX,{"derivedFrom":[makeQuery(id+"F4.boolean.opBoolean","COPY",EDGE,{"derivedFrom":makeQuery(id+"F4.opExtrude","TWEAK_EDGE",EDGE,{"derivedFrom":[subQ22,makeQuery(id+"F2.opShell","OFFSET_EDGE",EDGE,{"disambiguationData":[OSD([subQ2]),TDD([makeQuery(id+"F1.opExtrude","CAP_EDGE",EDGE,{"disambiguationData":[OSD([subQ2])],"isStart":true})])]})]})}),makeQuery(id+"F4.boolean.opBoolean","COPY",EDGE,{"derivedFrom":makeQuery(id+"F4.opExtrude","TWEAK_EDGE",EDGE,{"derivedFrom":[subQ22,makeQuery(id+"F2.opShell","OFFSET_EDGE",EDGE,{"disambiguationData":[OSD([subQ0]),TDD([makeQuery(id+"F1.opExtrude","CAP_EDGE",EDGE,{"disambiguationData":[OSD([subQ0])],"isStart":true})]),OD(0.0)]})]})})]})])]})]});}
            var Q2;
            {var subQ0=sQuery(id+"F0.wireOp",EDGE,"E5");var subQ1=sQuery(id+"F0.wireOp",EDGE,"E21");var subQ2=sQuery(id+"F0.wireOp",EDGE,"E20");var subQ3=sQuery(id+"F0.wireOp",EDGE,"E19");var subQ4=sQuery(id+"F0.wireOp",EDGE,"E18.right");var subQ5=sQuery(id+"F0.wireOp",EDGE,"E18.left");var subQ6=sQuery(id+"F0.wireOp",EDGE,"E17.right");var subQ7=sQuery(id+"F0.wireOp",EDGE,"E17.left");var subQ8=sQuery(id+"F0.wireOp",EDGE,"E16");var subQ9=sQuery(id+"F0.wireOp",EDGE,"E15");var subQ10=sQuery(id+"F0.wireOp",EDGE,"E14");var subQ11=sQuery(id+"F0.wireOp",EDGE,"E13");var subQ12=sQuery(id+"F0.wireOp",EDGE,"E12");var subQ13=sQuery(id+"F0.wireOp",EDGE,"E9.right");var subQ14=sQuery(id+"F0.wireOp",EDGE,"E9.left");var subQ15=sQuery(id+"F0.wireOp",EDGE,"E8.right");var subQ16=sQuery(id+"F0.wireOp",EDGE,"E8.left");var subQ17=sQuery(id+"F0.wireOp",EDGE,"E7");var subQ18=sQuery(id+"F0.wireOp",EDGE,"E6");var subQ19=sQuery(id+"F0.wireOp",EDGE,"E2.right");var subQ20=sQuery(id+"F0.wireOp",EDGE,"E2.left");var subQ21=sQuery(id+"F0.wireOp",EDGE,"E0");var subQ22=makeQuery(id+"F1.opExtrude","CAP_FACE",FACE,{"disambiguationData":[OSD([subQ21,subQ20,subQ19,subQ0,subQ18,subQ17,subQ16,subQ15,subQ14,subQ13,subQ12,subQ11,subQ10,subQ9,subQ8,subQ7,subQ6,subQ5,subQ4,subQ3,subQ2,subQ1])],"isStart":true});var subQ23=makeQuery(id+"F1.opExtrude","SWEPT_FACE",FACE,{"disambiguationData":[OSD([subQ11])]});var subQ24=makeQuery(id+"F1.opExtrude","SWEPT_FACE",FACE,{"disambiguationData":[OSD([subQ0])]});Q2=makeQuery(id+"F6.boolean.opBoolean","MERGE",EDGE,{"derivedFrom":[makeQuery(id+"F4.boolean.opBoolean","MERGE",EDGE,{"derivedFrom":[makeQuery(id+"F2.opShell","TWEAK_EDGE",EDGE,{"derivedFrom":[subQ24,subQ23]}),makeQuery(id+"F4.opExtrude","SWEPT_EDGE",EDGE,{"disambiguationData":[OSD([subQ21,subQ20,subQ19,subQ0,subQ18,subQ17,subQ16,subQ15,subQ14,subQ13,subQ12,subQ11,subQ10,subQ9,subQ8,subQ7,subQ6,subQ5,subQ4,subQ3,subQ2,subQ1]),TDD([makeQuery(id+"F2.opShell","TWEAK_VERTEX",VERTEX,{"derivedFrom":[subQ22,subQ24,subQ23]})])]})]}),makeQuery(id+"F6.opExtrude","SWEPT_EDGE",EDGE,{"disambiguationData":[OSD([subQ21,subQ20,subQ19,subQ0,subQ18,subQ17,subQ16,subQ15,subQ14,subQ13,subQ12,subQ11,subQ10,subQ9,subQ8,subQ7,subQ6,subQ5,subQ4,subQ3,subQ2,subQ1]),TDD([makeQuery(id+"F5.imprint","INTERSECT",VERTEX,{"derivedFrom":[makeQuery(id+"F4.boolean.opBoolean","COPY",EDGE,{"derivedFrom":makeQuery(id+"F4.opExtrude","TWEAK_EDGE",EDGE,{"derivedFrom":[subQ22,makeQuery(id+"F2.opShell","OFFSET_EDGE",EDGE,{"disambiguationData":[OSD([subQ11]),TDD([makeQuery(id+"F1.opExtrude","CAP_EDGE",EDGE,{"disambiguationData":[OSD([subQ11])],"isStart":true})])]})]})}),makeQuery(id+"F4.boolean.opBoolean","COPY",EDGE,{"derivedFrom":makeQuery(id+"F4.opExtrude","TWEAK_EDGE",EDGE,{"derivedFrom":[subQ22,makeQuery(id+"F2.opShell","OFFSET_EDGE",EDGE,{"disambiguationData":[OSD([subQ0]),TDD([makeQuery(id+"F1.opExtrude","CAP_EDGE",EDGE,{"disambiguationData":[OSD([subQ0])],"isStart":true})]),OD(0.0)]})]})})]})])]})]});}
            var Q3;
            {var subQ0=sQuery(id+"F0.wireOp",EDGE,"E5");var subQ1=sQuery(id+"F0.wireOp",EDGE,"E21");var subQ2=sQuery(id+"F0.wireOp",EDGE,"E20");var subQ3=sQuery(id+"F0.wireOp",EDGE,"E19");var subQ4=sQuery(id+"F0.wireOp",EDGE,"E18.right");var subQ5=sQuery(id+"F0.wireOp",EDGE,"E18.left");var subQ6=sQuery(id+"F0.wireOp",EDGE,"E17.right");var subQ7=sQuery(id+"F0.wireOp",EDGE,"E17.left");var subQ8=sQuery(id+"F0.wireOp",EDGE,"E16");var subQ9=sQuery(id+"F0.wireOp",EDGE,"E15");var subQ10=sQuery(id+"F0.wireOp",EDGE,"E14");var subQ11=sQuery(id+"F0.wireOp",EDGE,"E13");var subQ12=sQuery(id+"F0.wireOp",EDGE,"E12");var subQ13=sQuery(id+"F0.wireOp",EDGE,"E9.right");var subQ14=sQuery(id+"F0.wireOp",EDGE,"E9.left");var subQ15=sQuery(id+"F0.wireOp",EDGE,"E8.right");var subQ16=sQuery(id+"F0.wireOp",EDGE,"E8.left");var subQ17=sQuery(id+"F0.wireOp",EDGE,"E7");var subQ18=sQuery(id+"F0.wireOp",EDGE,"E6");var subQ19=sQuery(id+"F0.wireOp",EDGE,"E2.right");var subQ20=sQuery(id+"F0.wireOp",EDGE,"E2.left");var subQ21=sQuery(id+"F0.wireOp",EDGE,"E0");var subQ22=makeQuery(id+"F1.opExtrude","CAP_FACE",FACE,{"disambiguationData":[OSD([subQ21,subQ20,subQ19,subQ0,subQ18,subQ17,subQ16,subQ15,subQ14,subQ13,subQ12,subQ11,subQ10,subQ9,subQ8,subQ7,subQ6,subQ5,subQ4,subQ3,subQ2,subQ1])],"isStart":true});var subQ23=makeQuery(id+"F1.opExtrude","SWEPT_FACE",FACE,{"disambiguationData":[OSD([subQ1])]});var subQ24=makeQuery(id+"F1.opExtrude","SWEPT_FACE",FACE,{"disambiguationData":[OSD([subQ0])]});Q3=makeQuery(id+"F6.boolean.opBoolean","MERGE",EDGE,{"derivedFrom":[makeQuery(id+"F4.boolean.opBoolean","MERGE",EDGE,{"derivedFrom":[makeQuery(id+"F2.opShell","TWEAK_EDGE",EDGE,{"derivedFrom":[subQ24,subQ23]}),makeQuery(id+"F4.opExtrude","SWEPT_EDGE",EDGE,{"disambiguationData":[OSD([subQ21,subQ20,subQ19,subQ0,subQ18,subQ17,subQ16,subQ15,subQ14,subQ13,subQ12,subQ11,subQ10,subQ9,subQ8,subQ7,subQ6,subQ5,subQ4,subQ3,subQ2,subQ1]),TDD([makeQuery(id+"F2.opShell","TWEAK_VERTEX",VERTEX,{"derivedFrom":[subQ22,subQ24,subQ23]})])]})]}),makeQuery(id+"F6.opExtrude","SWEPT_EDGE",EDGE,{"disambiguationData":[OSD([subQ21,subQ20,subQ19,subQ0,subQ18,subQ17,subQ16,subQ15,subQ14,subQ13,subQ12,subQ11,subQ10,subQ9,subQ8,subQ7,subQ6,subQ5,subQ4,subQ3,subQ2,subQ1]),TDD([makeQuery(id+"F5.imprint","INTERSECT",VERTEX,{"derivedFrom":[makeQuery(id+"F4.boolean.opBoolean","COPY",EDGE,{"derivedFrom":makeQuery(id+"F4.opExtrude","TWEAK_EDGE",EDGE,{"derivedFrom":[subQ22,makeQuery(id+"F2.opShell","OFFSET_EDGE",EDGE,{"disambiguationData":[OSD([subQ1]),TDD([makeQuery(id+"F1.opExtrude","CAP_EDGE",EDGE,{"disambiguationData":[OSD([subQ1])],"isStart":true})])]})]})}),makeQuery(id+"F4.boolean.opBoolean","COPY",EDGE,{"derivedFrom":makeQuery(id+"F4.opExtrude","TWEAK_EDGE",EDGE,{"derivedFrom":[subQ22,makeQuery(id+"F2.opShell","OFFSET_EDGE",EDGE,{"disambiguationData":[OSD([subQ0]),TDD([makeQuery(id+"F1.opExtrude","CAP_EDGE",EDGE,{"disambiguationData":[OSD([subQ0])],"isStart":true})]),OD(0.0)]})]})})]})])]})]});}
            fillet(context, id + "F9", {"entities" : qUnion([Q0, Q1, Q2, Q3]), "radius" : 0.76 * mm, "tangentPropagation" : true, "allowEdgeOverflow" : false});
        }
    });
